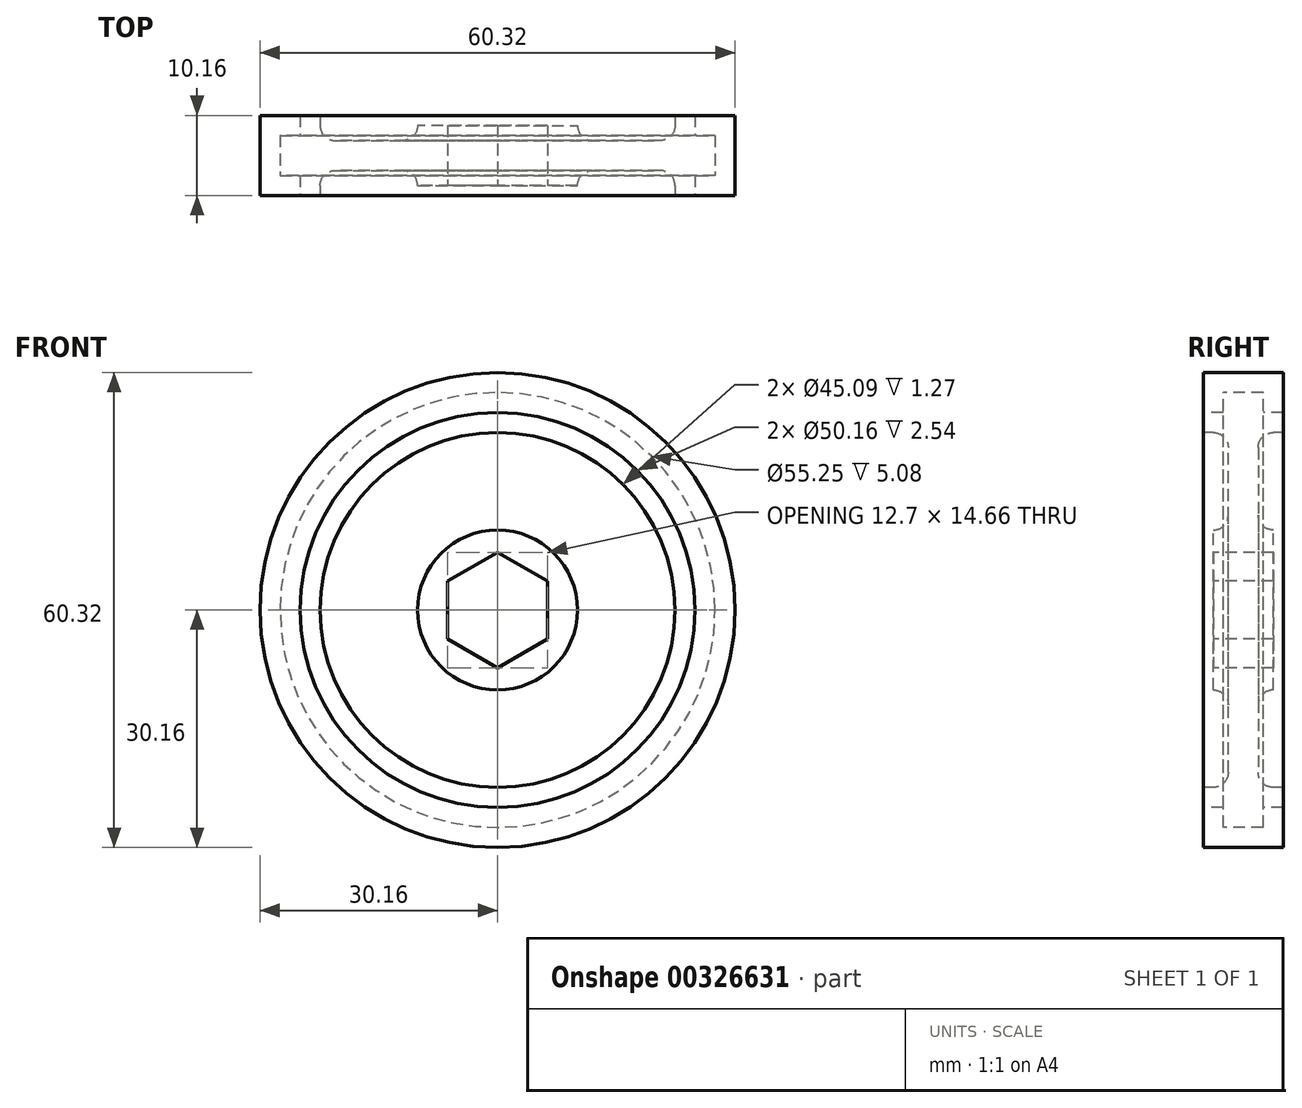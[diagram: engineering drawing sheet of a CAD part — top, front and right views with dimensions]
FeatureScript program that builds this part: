
annotation { "Feature Type Name" : "Feature", "Feature Type Description" : "" }
export const myFeature = defineFeature(function(context is Context, id is Id, definition is map)
    precondition{}
    {
        {
            var Q0;
            Q0=qCreatedBy(makeId("Right.planeOp"),FACE);
            var sketch = newSketch(context, id + "F0", { "sketchPlane" : qUnion([Q0])});
            skLineSegment(sketch, "E0", {"start": v(-3.8, 0) * mm, "end": v(3.8, 0) * mm, "construction": true});
            skLineSegment(sketch, "E1", {"start": v(-3.81, 0) * mm, "end": v(-3.81, 10.16) * mm});
            skLineSegment(sketch, "E2", {"start": v(-3.8, 10.16) * mm, "end": v(-1.9, 10.16) * mm});
            skLineSegment(sketch, "E3", {"start": v(-1.9, 10.16) * mm, "end": v(-1.9, 22.54) * mm});
            skLineSegment(sketch, "E4", {"start": v(-1.9, 22.54) * mm, "end": v(-5.08, 22.54) * mm});
            skLineSegment(sketch, "E5", {"start": v(-5.08, 22.54) * mm, "end": v(-5.08, 25.08) * mm});
            skLineSegment(sketch, "E6", {"start": v(-5.08, 25.08) * mm, "end": v(-2.54, 25.08) * mm});
            skLineSegment(sketch, "E7", {"start": v(-2.54, 25.08) * mm, "end": v(-2.54, 27.62) * mm});
            skLineSegment(sketch, "E8", {"start": v(-2.54, 27.62) * mm, "end": v(2.54, 27.62) * mm});
            skLineSegment(sketch, "E9", {"start": v(2.54, 27.62) * mm, "end": v(2.54, 25.08) * mm});
            skLineSegment(sketch, "E10", {"start": v(2.54, 25.08) * mm, "end": v(5.08, 25.08) * mm});
            skLineSegment(sketch, "E11", {"start": v(5.08, 25.08) * mm, "end": v(5.08, 22.54) * mm});
            skLineSegment(sketch, "E12", {"start": v(5.08, 22.54) * mm, "end": v(1.9, 22.54) * mm});
            skLineSegment(sketch, "E13", {"start": v(1.9, 22.54) * mm, "end": v(1.9, 10.16) * mm});
            skLineSegment(sketch, "E14", {"start": v(1.9, 10.16) * mm, "end": v(3.8, 10.16) * mm});
            skLineSegment(sketch, "E15", {"start": v(3.81, 10.16) * mm, "end": v(3.81, 0) * mm});
            skLineSegment(sketch, "E16", {"start": v(-3.8, 0) * mm, "end": v(3.8, 0) * mm});
            skSolve(sketch);
        }
        {
            var Q0;
            Q0 = qSketchRegion(id + "F0", true);
            var Q1;
            Q1=sQuery(id+"F0.wireOp",EDGE,"E16");
            revolve(context, id + "F1", {"entities" : qUnion([Q0]), "axis" : qUnion([Q1]), "revolveType" : RevolveType.FULL});
        }
        {
            var Q0;
            Q0=makeQuery(id+"F1.opRevolve","SWEPT_EDGE",EDGE,{"disambiguationData":[OSD([sQuery(id+"F0.wireOp",EDGE,"E13"),sQuery(id+"F0.wireOp",EDGE,"E14")])]});
            var Q1;
            Q1=makeQuery(id+"F1.opRevolve","SWEPT_EDGE",EDGE,{"disambiguationData":[OSD([sQuery(id+"F0.wireOp",EDGE,"E12"),sQuery(id+"F0.wireOp",EDGE,"E13")])]});
            var Q2;
            Q2=makeQuery(id+"F1.opRevolve","SWEPT_EDGE",EDGE,{"disambiguationData":[OSD([sQuery(id+"F0.wireOp",EDGE,"E2"),sQuery(id+"F0.wireOp",EDGE,"E3")])]});
            var Q3;
            Q3=makeQuery(id+"F1.opRevolve","SWEPT_EDGE",EDGE,{"disambiguationData":[OSD([sQuery(id+"F0.wireOp",EDGE,"E3"),sQuery(id+"F0.wireOp",EDGE,"E4")])]});
            fillet(context, id + "F2", {"entities" : qUnion([Q0, Q1, Q2, Q3]), "radius" : 3.8 * mm / 2, "tangentPropagation" : true, "allowEdgeOverflow" : false});
        }
        {
            var Q0;
            Q0=makeQuery(id+"F1.opRevolve","SWEPT_FACE",FACE,{"disambiguationData":[OSD([sQuery(id+"F0.wireOp",EDGE,"E1")])]});
            var sketch = newSketch(context, id + "F3", { "sketchPlane" : qUnion([Q0])});
            skCircle(sketch, "E17.cCircle", {"center": v(0, 0) * mm, "radius": 6.35 * mm, "construction": true});
            skLineSegment(sketch, "E17.0", {"start": v(6.35, 3.67) * mm, "end": v(6.35, -3.67) * mm});
            skLineSegment(sketch, "E17.1", {"start": v(6.35, -3.67) * mm, "end": v(0, -7.33) * mm});
            skLineSegment(sketch, "E17.2", {"start": v(0, -7.33) * mm, "end": v(-6.35, -3.67) * mm});
            skLineSegment(sketch, "E17.3", {"start": v(-6.35, -3.67) * mm, "end": v(-6.35, 3.67) * mm});
            skLineSegment(sketch, "E17.4", {"start": v(-6.35, 3.67) * mm, "end": v(0, 7.33) * mm});
            skLineSegment(sketch, "E17.5", {"start": v(0, 7.33) * mm, "end": v(6.35, 3.67) * mm});
            skPoint(sketch, "E17.0.midPoint", {"position": v(6.35, 0) * mm});
            skSolve(sketch);
        }
        {
            var Q0;
            Q0 = qSketchRegion(id + "F3", true);
            extrude(context, id + "F4", {"entities" : qUnion([Q0]), "operationType" : NewBodyOperationType.REMOVE, "endBound" : BoundingType.UP_TO_NEXT, "oppositeDirection" : true, "depth" : 25 * mm});
        }
        {
            var Q0;
            Q0=qCreatedBy(makeId("Right.planeOp"),FACE);
            var sketch = newSketch(context, id + "F5", { "sketchPlane" : qUnion([Q0])});
            skLineSegment(sketch, "E18", {"start": v(-5.08, 25.08) * mm, "end": v(-2.54, 25.08) * mm});
            skLineSegment(sketch, "E19", {"start": v(-2.54, 25.08) * mm, "end": v(-2.54, 27.62) * mm});
            skLineSegment(sketch, "E20", {"start": v(-2.54, 27.62) * mm, "end": v(2.54, 27.62) * mm});
            skLineSegment(sketch, "E21", {"start": v(2.54, 27.62) * mm, "end": v(2.54, 25.08) * mm});
            skLineSegment(sketch, "E22", {"start": v(2.54, 25.08) * mm, "end": v(5.08, 25.08) * mm});
            skLineSegment(sketch, "E23", {"start": v(5.08, 25.08) * mm, "end": v(5.08, 30.16) * mm});
            skLineSegment(sketch, "E24", {"start": v(5.08, 30.16) * mm, "end": v(-5.08, 30.16) * mm});
            skLineSegment(sketch, "E25", {"start": v(-5.08, 30.16) * mm, "end": v(-5.08, 25.08) * mm});
            skSolve(sketch);
        }
        {
            var Q0;
            Q0 = qSketchRegion(id + "F5", true);
            var Q1;
            Q1=sQuery(id+"F0.wireOp",EDGE,"E16");
            revolve(context, id + "F6", {"entities" : qUnion([Q0]), "axis" : qUnion([Q1]), "revolveType" : RevolveType.FULL});
        }
    });
